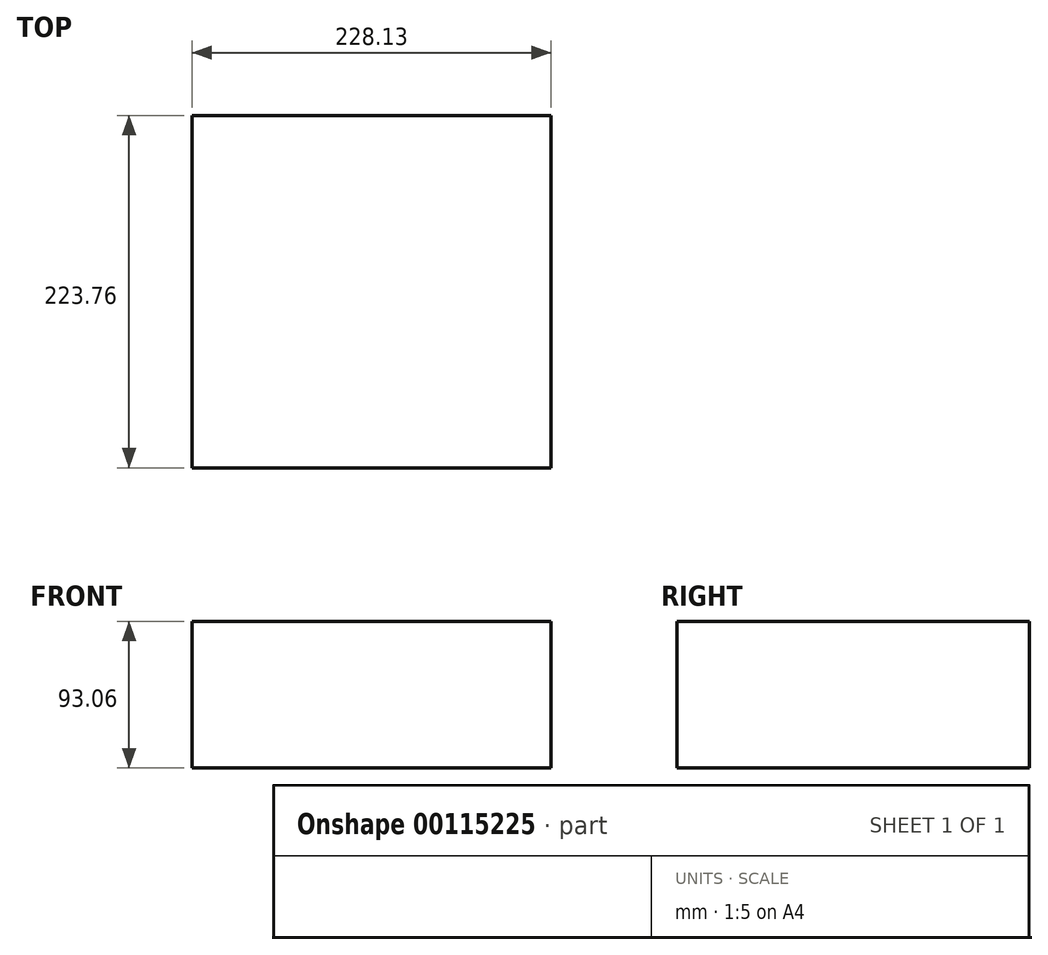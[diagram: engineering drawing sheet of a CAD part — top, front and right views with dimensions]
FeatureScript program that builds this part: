
annotation { "Feature Type Name" : "Feature", "Feature Type Description" : "" }
export const myFeature = defineFeature(function(context is Context, id is Id, definition is map)
    precondition{}
    {
        {
            var Q0;
            Q0=qCreatedBy(makeId("Top.planeOp"),FACE);
            var sketch = newSketch(context, id + "F0", { "sketchPlane" : qUnion([Q0])});
            skLineSegment(sketch, "E0.bottom", {"start": v(-132.6, -109.66) * mm, "end": v(-67.77, -109.66) * mm});
            skLineSegment(sketch, "E0.top", {"start": v(-132.6, -113.68) * mm, "end": v(-67.77, -113.68) * mm});
            skLineSegment(sketch, "E0.left", {"start": v(-132.6, -109.66) * mm, "end": v(-132.6, -113.68) * mm});
            skLineSegment(sketch, "E0.right", {"start": v(-67.77, -109.66) * mm, "end": v(-67.77, -113.68) * mm});
            skLineSegment(sketch, "E1.bottom", {"start": v(-228.13, -127.16) * mm, "end": v(0, -127.16) * mm});
            skLineSegment(sketch, "E1.top", {"start": v(-228.13, 96.6) * mm, "end": v(0, 96.6) * mm});
            skLineSegment(sketch, "E1.left", {"start": v(-228.13, -127.16) * mm, "end": v(-228.13, 96.6) * mm});
            skLineSegment(sketch, "E1.right", {"start": v(0, -127.16) * mm, "end": v(0, 96.6) * mm});
            skSolve(sketch);
        }
        {
            var Q0;
            Q0=makeQuery(id+"F0.imprint","IMPRINT",FACE,{"disambiguationData":[TD([[makeQuery(id+"F0.imprint","IMPRINT",EDGE,{"derivedFrom":sQuery(id+"F0.wireOp",EDGE,"E0.bottom")}),-1.0]])]});
            var Q1;
            Q1=makeQuery(id+"F0.imprint","IMPRINT",FACE,{"disambiguationData":[TD([[makeQuery(id+"F0.imprint","IMPRINT",EDGE,{"derivedFrom":sQuery(id+"F0.wireOp",EDGE,"E0.bottom")}),1.0]])]});
            extrude(context, id + "F1", {"entities" : qUnion([Q0, Q1]), "depth" : 93.06 * mm});
        }
    });
